# Revit family: Specialty_Equipment-Bavis_Fabacraft-Electric_Transaction_Drawer
name_source: partatom
category: Specialty Equipment
units: mm (PartAtom-declared; Revit-internal decimal feet)

## family parameters
Always vertical = Yes
Cut with Voids When Loaded = Yes
Host = Wall
OmniClass Number = 23.40.70.27.24.21
OmniClass Title = Service and Teller Window Units
Part Type = Normal
Room Calculation Point = No
Round Connector Dimension = Use Diameter
Shared = No

## types (3) — shared parameters
Apparent Load = 0 VA
Assembly Code = E1010
C Drawer = 0' - 0"
C Inset = 0' - 0"
Default Elevation = 0' - 0"
Description = Electric Transactions Drawers
Drawer = Paint - Bavis Fabacraft - Red
Elevation Height = 3' - 0"
Finish = Metal - Bavis Fabacraft - Aluminum - Dark Grey
Hardware = Metal - Bavis Fabacraft - Steel
Keynote = 14 90 00
Load Classification = Power
Manufacturer = Bavis Fabacraft
Model = See Order Code
Number of Poles = 1
Power Factor = 1
Product Documentation Link = https://docs.bavis.com
Product Name = Bavis Electric Transactions Drawers
Product Page URL = https://www.bavis.com
URL = https://www.bavis.com
Version = 2020 - v1.0a
Video Link = https://www.youtube.com
Voltage = 120 V

## per-type parameters (varying)
| type | C Back | C Counter Open Length | C Counter Open Width | C Door Height | C Door Width | C Middle | C Rough Height | C Rough Width | C Sign Constraint | C Start | C Stroke | C Void Start | Height | Instruction Sheet Link | Length | Width |
| Extra Small | 0' - 11 3/4" | 0' - 8 5/8" | 1' - 2 7/8" | 0' - 7 1/16" | 1' - 3 1/2" | 0' - 7 1/2" | 0' - 6 3/4" | 1' - 2 3/4" | 1 | 0' - 7 3/8" | 0' - 11 1/2" | 0' - 6 3/8" | 0' - 6 9/16" | https://docs.bavis.com | 2' - 2 1/2" | 1' - 2 1/2" |
| Small | 0' - 10 7/8" | 0' - 10" | 1' - 3 5/8" | 0' - 9 1/2" | 1' - 4 5/8" | 0' - 9 1/16" | 0' - 9 1/4" | 1' - 4" | 2 | 0' - 9 1/16" | 0' - 11 1/2" | 0' - 8 7/8" | 0' - 9" | https://docs.bavis.com | 2' - 5" | 1' - 3 5/8" |
| Large | 0' - 10 5/16" | 0' - 11" | 1' - 3 3/4" | 0' - 11" | 1' - 4 5/8" | 0' - 9 3/8" | 0' - 10 3/4" | 1' - 4" | 3 | 0' - 9 5/16" | 1' - 5 1/2" | 0' - 8 1/2" | 0' - 10 1/2" | Please Contact Manufacturer for Instruction Documentation | 2' - 5" | 1' - 3 5/8" |

## geometry (parser evidence)
native form markers: Sweep x11
no freeform markers — native parametric forms only
